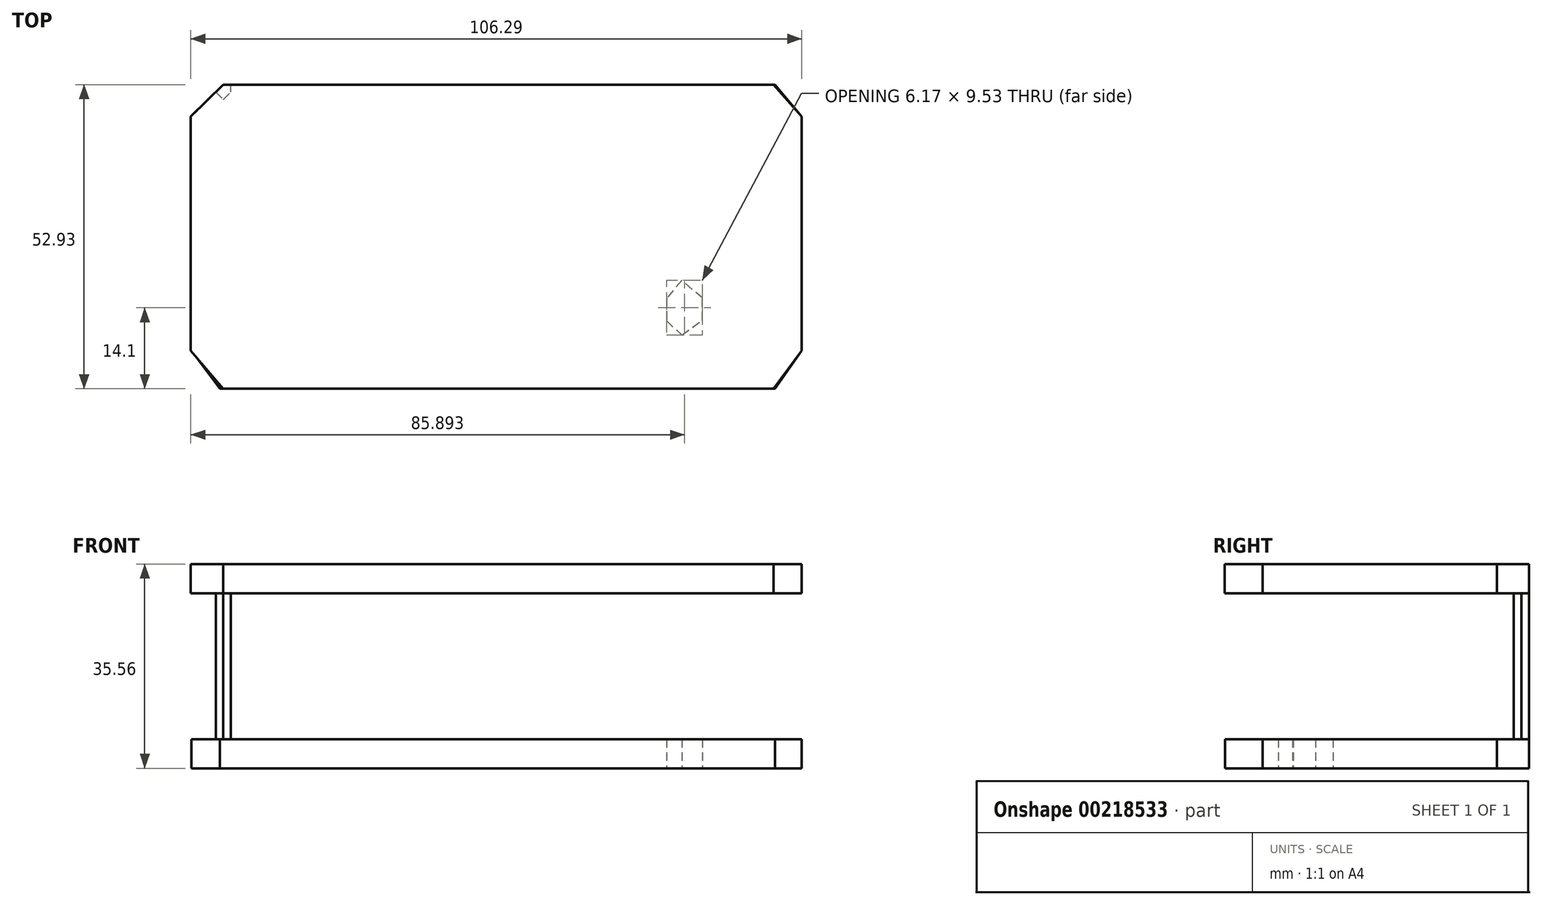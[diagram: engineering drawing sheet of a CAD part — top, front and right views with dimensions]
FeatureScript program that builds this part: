
annotation { "Feature Type Name" : "Feature", "Feature Type Description" : "" }
export const myFeature = defineFeature(function(context is Context, id is Id, definition is map)
    precondition{}
    {
        {
            var Q0;
            Q0=qCreatedBy(makeId("Top.planeOp"),FACE);
            var sketch = newSketch(context, id + "F0", { "sketchPlane" : qUnion([Q0])});
            skLineSegment(sketch, "E0", {"start": v(-48.65, 46.3) * mm, "end": v(47.3, 46.3) * mm});
            skLineSegment(sketch, "E1", {"start": v(47.3, 46.3) * mm, "end": v(51.98, 40.74) * mm});
            skLineSegment(sketch, "E2", {"start": v(51.98, 40.74) * mm, "end": v(51.98, 0) * mm});
            skLineSegment(sketch, "E3", {"start": v(51.98, 0) * mm, "end": v(47.3, -6.58) * mm});
            skLineSegment(sketch, "E4", {"start": v(47.3, -6.58) * mm, "end": v(-49.24, -6.58) * mm});
            skLineSegment(sketch, "E5", {"start": v(-49.24, -6.58) * mm, "end": v(-54.2, 0) * mm});
            skLineSegment(sketch, "E6", {"start": v(-54.2, 0) * mm, "end": v(-54.2, 40.74) * mm});
            skLineSegment(sketch, "E7", {"start": v(-54.2, 40.74) * mm, "end": v(-48.65, 46.3) * mm});
            skLineSegment(sketch, "E8.MirrorCS", {"start": v(-94.95, 146.94) * mm, "end": v(-101.53, 142.26) * mm});
            skLineSegment(sketch, "E9.MirrorCS", {"start": v(-48.65, 142.26) * mm, "end": v(-54.2, 146.94) * mm});
            skSolve(sketch);
        }
        {
            var Q0;
            Q0 = qSketchRegion(id + "F0", true);
            extrude(context, id + "F1", {"entities" : qUnion([Q0]), "depth" : 5.08 * mm});
        }
        {
            var Q0;
            Q0=makeQuery(id+"F1.opExtrude","CAP_FACE",FACE,{"disambiguationData":[OSD([sQuery(id+"F0.wireOp",EDGE,"E0"),sQuery(id+"F0.wireOp",EDGE,"E1"),sQuery(id+"F0.wireOp",EDGE,"E2"),sQuery(id+"F0.wireOp",EDGE,"E3"),sQuery(id+"F0.wireOp",EDGE,"E4"),sQuery(id+"F0.wireOp",EDGE,"E5"),sQuery(id+"F0.wireOp",EDGE,"E6"),sQuery(id+"F0.wireOp",EDGE,"E7")])],"isStart":false});
            var sketch = newSketch(context, id + "F2", { "sketchPlane" : qUnion([Q0])});
            skLineSegment(sketch, "E10", {"start": v(-49.96, 45) * mm, "end": v(-48.65, 43.68) * mm});
            skLineSegment(sketch, "E11", {"start": v(-48.65, 43.68) * mm, "end": v(-47.32, 45) * mm});
            skLineSegment(sketch, "E12", {"start": v(-47.32, 45) * mm, "end": v(-47.32, 46.3) * mm});
            skLineSegment(sketch, "E13", {"start": v(-47.32, 46.3) * mm, "end": v(-48.65, 46.3) * mm});
            skLineSegment(sketch, "E14", {"start": v(-48.65, 46.3) * mm, "end": v(-49.96, 45) * mm});
            skSolve(sketch);
        }
        {
            var Q0;
            Q0 = qSketchRegion(id + "F2", true);
            extrude(context, id + "F3", {"entities" : qUnion([Q0]), "operationType" : NewBodyOperationType.ADD, "depth" : 25.4 * mm});
        }
        {
            var Q0;
            Q0=makeQuery(id+"F3.opExtrude","CAP_FACE",FACE,{"disambiguationData":[OSD([sQuery(id+"F2.wireOp",EDGE,"E10"),sQuery(id+"F2.wireOp",EDGE,"E11"),sQuery(id+"F2.wireOp",EDGE,"E12"),sQuery(id+"F2.wireOp",EDGE,"E13"),sQuery(id+"F2.wireOp",EDGE,"E14")])],"isStart":false});
            var sketch = newSketch(context, id + "F4", { "sketchPlane" : qUnion([Q0])});
            skLineSegment(sketch, "E15", {"start": v(-48.65, 46.3) * mm, "end": v(47.1, 46.3) * mm});
            skLineSegment(sketch, "E16", {"start": v(47.1, 46.3) * mm, "end": v(51.95, 40.74) * mm});
            skLineSegment(sketch, "E17", {"start": v(51.95, 40.74) * mm, "end": v(51.95, 0) * mm});
            skLineSegment(sketch, "E18", {"start": v(51.95, 0) * mm, "end": v(47.1, -6.63) * mm});
            skLineSegment(sketch, "E19", {"start": v(47.1, -6.63) * mm, "end": v(-48.65, -6.63) * mm});
            skLineSegment(sketch, "E20", {"start": v(-48.65, -6.63) * mm, "end": v(-54.31, 0) * mm});
            skLineSegment(sketch, "E21", {"start": v(-54.31, 0) * mm, "end": v(-54.31, 40.74) * mm});
            skLineSegment(sketch, "E22", {"start": v(-54.31, 40.74) * mm, "end": v(-48.65, 46.3) * mm});
            skSolve(sketch);
        }
        {
            var Q0;
            Q0 = qSketchRegion(id + "F4", true);
            extrude(context, id + "F5", {"entities" : qUnion([Q0]), "operationType" : NewBodyOperationType.ADD, "depth" : 5.08 * mm});
        }
        {
            var Q0;
            Q0=makeQuery(id+"F1.opExtrude","CAP_FACE",FACE,{"disambiguationData":[OSD([sQuery(id+"F0.wireOp",EDGE,"E0"),sQuery(id+"F0.wireOp",EDGE,"E1"),sQuery(id+"F0.wireOp",EDGE,"E2"),sQuery(id+"F0.wireOp",EDGE,"E3"),sQuery(id+"F0.wireOp",EDGE,"E4"),sQuery(id+"F0.wireOp",EDGE,"E5"),sQuery(id+"F0.wireOp",EDGE,"E6"),sQuery(id+"F0.wireOp",EDGE,"E7")])],"isStart":true});
            var sketch = newSketch(context, id + "F6", { "sketchPlane" : qUnion([Q0])});
            skLineSegment(sketch, "E23", {"start": v(34.67, -5.3) * mm, "end": v(34.67, -9.18) * mm});
            skLineSegment(sketch, "E24", {"start": v(34.67, -9.18) * mm, "end": v(31.11, -12.23) * mm});
            skLineSegment(sketch, "E25", {"start": v(31.11, -12.23) * mm, "end": v(28.5, -9.18) * mm});
            skLineSegment(sketch, "E26", {"start": v(28.5, -9.18) * mm, "end": v(28.5, -5.18) * mm});
            skLineSegment(sketch, "E27", {"start": v(28.5, -5.18) * mm, "end": v(31.11, -2.7) * mm});
            skLineSegment(sketch, "E28", {"start": v(31.11, -2.7) * mm, "end": v(34.67, -5.3) * mm});
            skSolve(sketch);
        }
        {
            var Q0;
            Q0 = qSketchRegion(id + "F6", true);
            extrude(context, id + "F7", {"entities" : qUnion([Q0]), "operationType" : NewBodyOperationType.REMOVE, "oppositeDirection" : true, "depth" : 5.08 * mm});
        }
    });
